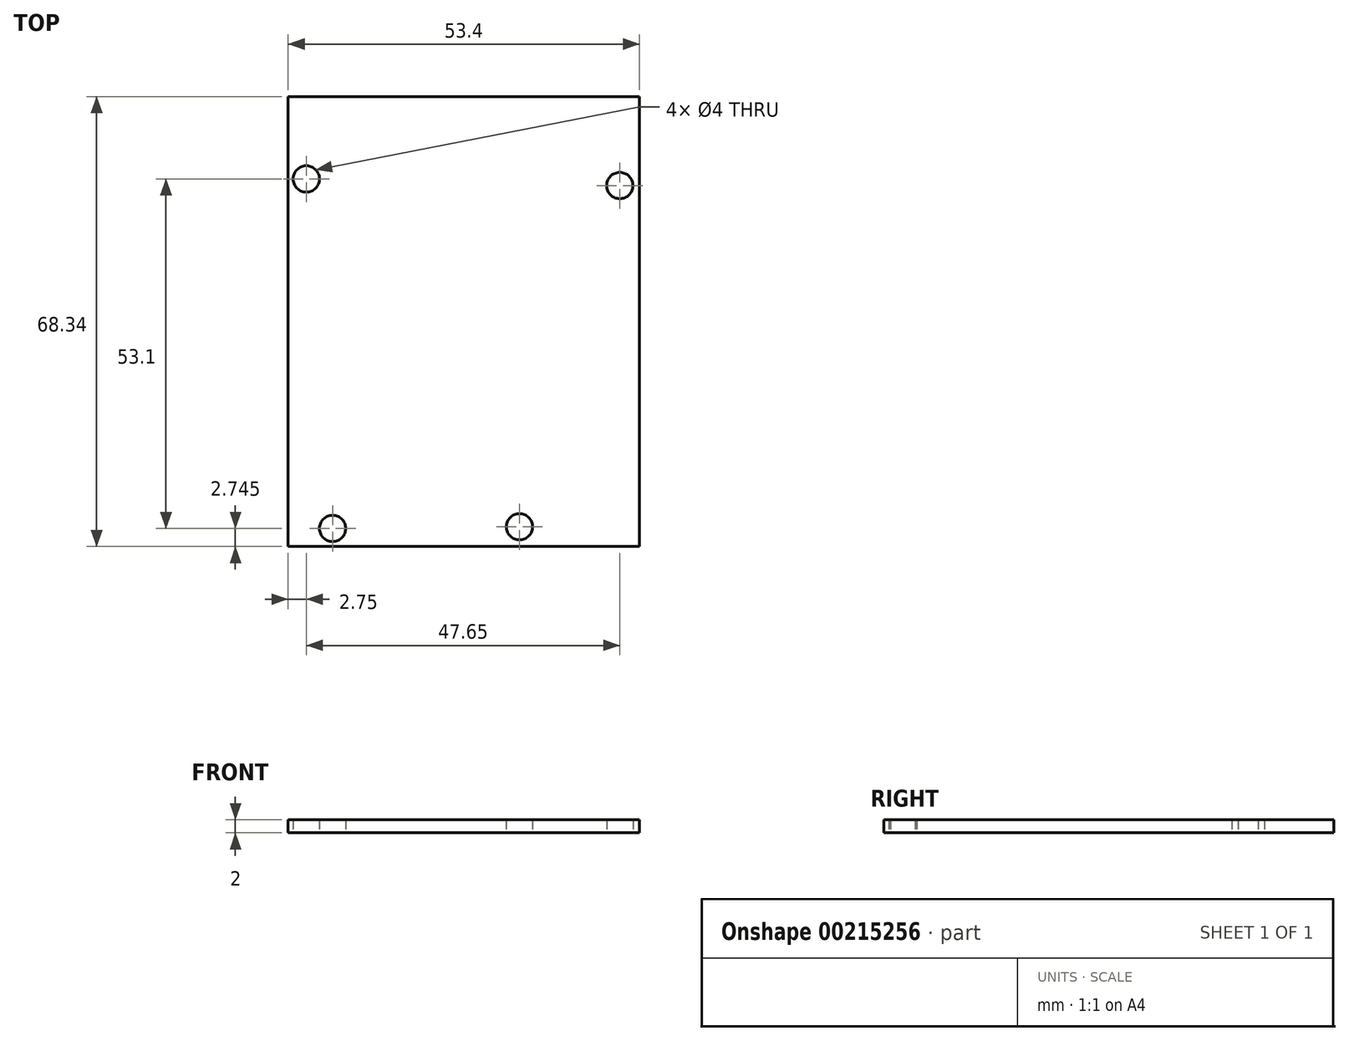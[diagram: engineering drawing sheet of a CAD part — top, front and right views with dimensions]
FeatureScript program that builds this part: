
annotation { "Feature Type Name" : "Feature", "Feature Type Description" : "" }
export const myFeature = defineFeature(function(context is Context, id is Id, definition is map)
    precondition{}
    {
        {
            var Q0;
            Q0=qCreatedBy(makeId("Top.planeOp"),FACE);
            var sketch = newSketch(context, id + "F0", { "sketchPlane" : qUnion([Q0])});
            skLineSegment(sketch, "E0.bottom", {"start": v(26.7, 34.17) * mm, "end": v(-26.7, 34.17) * mm});
            skLineSegment(sketch, "E0.top", {"start": v(26.7, -34.17) * mm, "end": v(-26.7, -34.17) * mm});
            skLineSegment(sketch, "E0.left", {"start": v(26.7, 34.17) * mm, "end": v(26.7, -34.17) * mm});
            skLineSegment(sketch, "E0.right", {"start": v(-26.7, 34.17) * mm, "end": v(-26.7, -34.17) * mm});
            skPoint(sketch, "E0.middle", {"position": v(0, 0) * mm});
            skLineSegment(sketch, "E1", {"start": v(-26.7, 34.17) * mm, "end": v(-26.7, 21.67) * mm});
            skLineSegment(sketch, "E2", {"start": v(-26.7, 21.67) * mm, "end": v(-23.95, 21.67) * mm});
            skCircle(sketch, "E3", {"center": v(-23.95, 21.67) * mm, "radius": 2 * mm});
            skLineSegment(sketch, "E4", {"start": v(26.7, 34.17) * mm, "end": v(26.7, 20.67) * mm});
            skLineSegment(sketch, "E5", {"start": v(26.7, 20.67) * mm, "end": v(23.7, 20.67) * mm});
            skCircle(sketch, "E6", {"center": v(23.7, 20.67) * mm, "radius": 2 * mm});
            skLineSegment(sketch, "E7", {"start": v(26.7, -34.17) * mm, "end": v(8.45, -34.17) * mm});
            skLineSegment(sketch, "E8", {"start": v(8.45, -34.17) * mm, "end": v(8.45, -31.17) * mm});
            skCircle(sketch, "E9", {"center": v(8.45, -31.17) * mm, "radius": 2 * mm});
            skLineSegment(sketch, "E10", {"start": v(-26.7, -34.17) * mm, "end": v(-19.95, -34.17) * mm});
            skLineSegment(sketch, "E11", {"start": v(-19.95, -34.17) * mm, "end": v(-19.95, -31.42) * mm});
            skCircle(sketch, "E12", {"center": v(-19.95, -31.42) * mm, "radius": 2 * mm});
            skLineSegment(sketch, "E13", {"start": v(-19.95, -31.42) * mm, "end": v(-19.95, 21.68) * mm, "construction": true});
            skLineSegment(sketch, "E14", {"start": v(-19.95, 21.68) * mm, "end": v(-23.95, 21.67) * mm, "construction": true});
            skSolve(sketch);
        }
        {
            var Q0;
            Q0=makeQuery(id+"F0.imprint","IMPRINT",FACE,{"disambiguationData":[TD([[makeQuery(id+"F0.imprint","IMPRINT",EDGE,{"derivedFrom":sQuery(id+"F0.wireOp",EDGE,"E0.bottom")}),1.0]])]});
            extrude(context, id + "F1", {"entities" : qUnion([Q0]), "depth" : 2 * mm});
        }
    });
